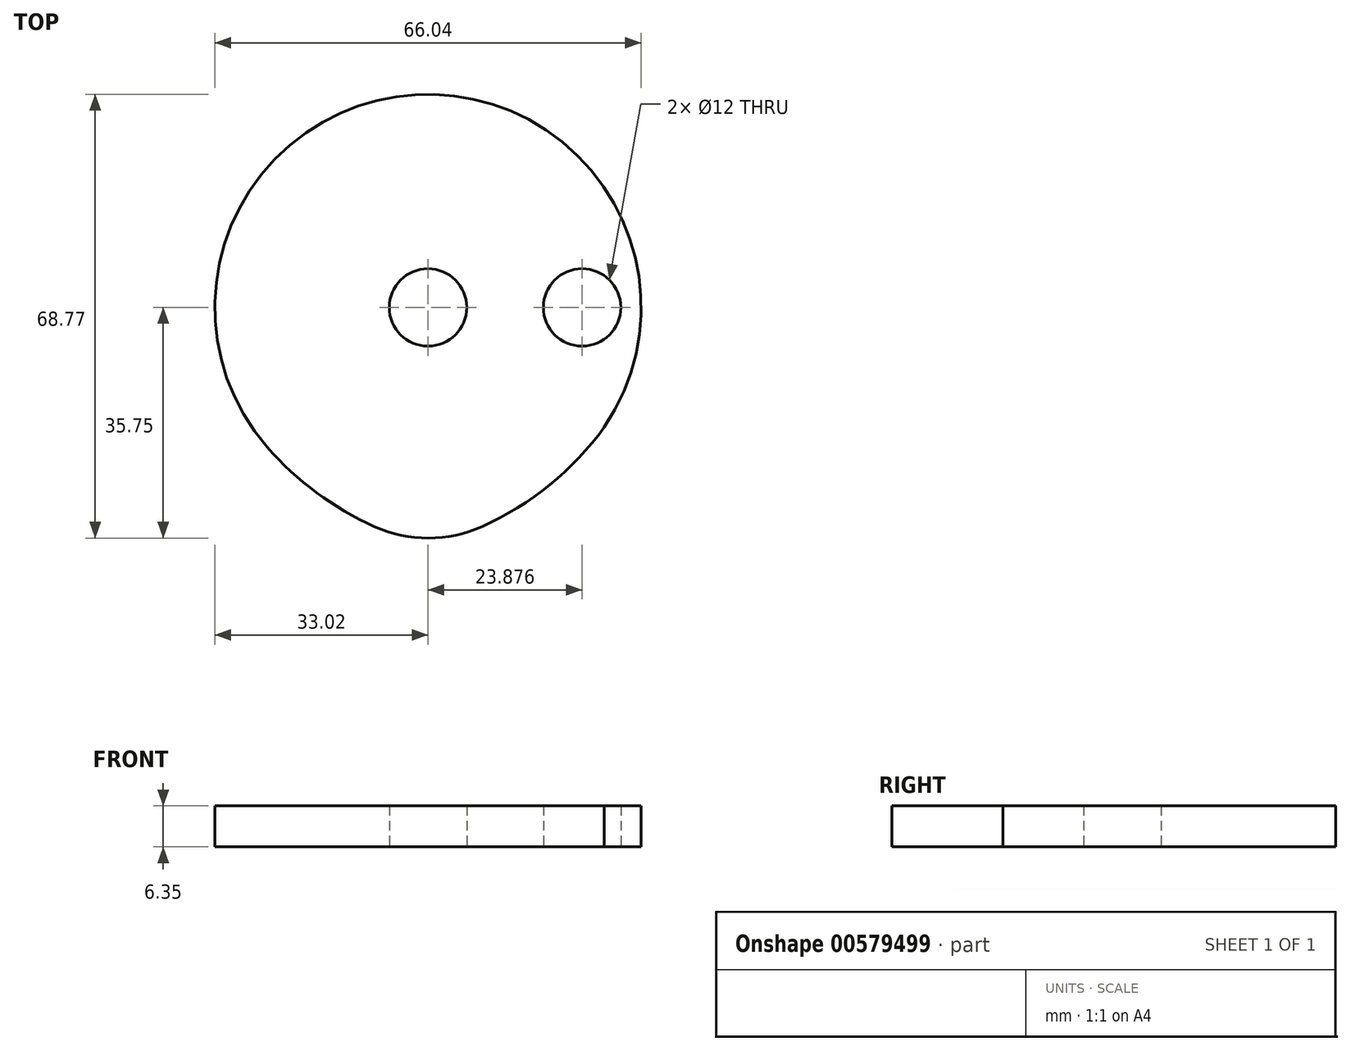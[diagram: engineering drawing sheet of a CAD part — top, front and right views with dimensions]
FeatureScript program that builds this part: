
annotation { "Feature Type Name" : "Feature", "Feature Type Description" : "" }
export const myFeature = defineFeature(function(context is Context, id is Id, definition is map)
    precondition{}
    {
        {
            var Q0;
            Q0=qCreatedBy(makeId("Top.planeOp"),FACE);
            var sketch = newSketch(context, id + "F0", { "sketchPlane" : qUnion([Q0])});
            skArc(sketch, "E0", {"start": v(27.31, -18.56) * mm, "mid": v(-1.96, 32.96) * mm, "end": v(-24.92, -21.66) * mm});
            skLineSegment(sketch, "E1", {"start": v(0, -33.02) * mm, "end": v(0, 6) * mm});
            skCircle(sketch, "E2", {"center": v(0, 0) * mm, "radius": 6 * mm});
            skLineSegment(sketch, "E3", {"start": v(0, -33.02) * mm, "end": v(0, -36.83) * mm});
            skArc(sketch, "E4", {"start": v(-24.92, -21.66) * mm, "mid": v(-13.62, -31.15) * mm, "end": v(0, -36.83) * mm});
            skArc(sketch, "E5", {"start": v(0, -36.83) * mm, "mid": v(15.3, -30.14) * mm, "end": v(27.31, -18.56) * mm});
            skLineSegment(sketch, "E6", {"start": v(0, 0) * mm, "end": v(0, 6) * mm});
            skLineSegment(sketch, "E7", {"start": v(0, 0) * mm, "end": v(6, 0) * mm});
            skLineSegment(sketch, "E8", {"start": v(0, 0) * mm, "end": v(23.88, 0) * mm});
            skCircle(sketch, "E9", {"center": v(23.88, 0) * mm, "radius": 6 * mm});
            skSolve(sketch);
        }
        {
            var Q0;
            Q0=makeQuery(id+"F0.imprint","IMPRINT",FACE,{"disambiguationData":[TD([[makeQuery(id+"F0.imprint","IMPRINT",EDGE,{"derivedFrom":sQuery(id+"F0.wireOp",EDGE,"E0")}),1.0]])]});
            extrude(context, id + "F1", {"entities" : qUnion([Q0]), "depth" : 6.35 * mm, "offsetDistance" : 25.4 * mm});
        }
        {
            var Q0;
            Q0=makeQuery(id+"F1.opExtrude","SWEPT_EDGE",EDGE,{"disambiguationData":[OSD([sQuery(id+"F0.wireOp",EDGE,"E4"),sQuery(id+"F0.wireOp",EDGE,"E5")])]});
            fillet(context, id + "F2", {"entities" : qUnion([Q0]), "radius" : 20.32 * mm, "tangentPropagation" : true, "allowEdgeOverflow" : false});
        }
    });
